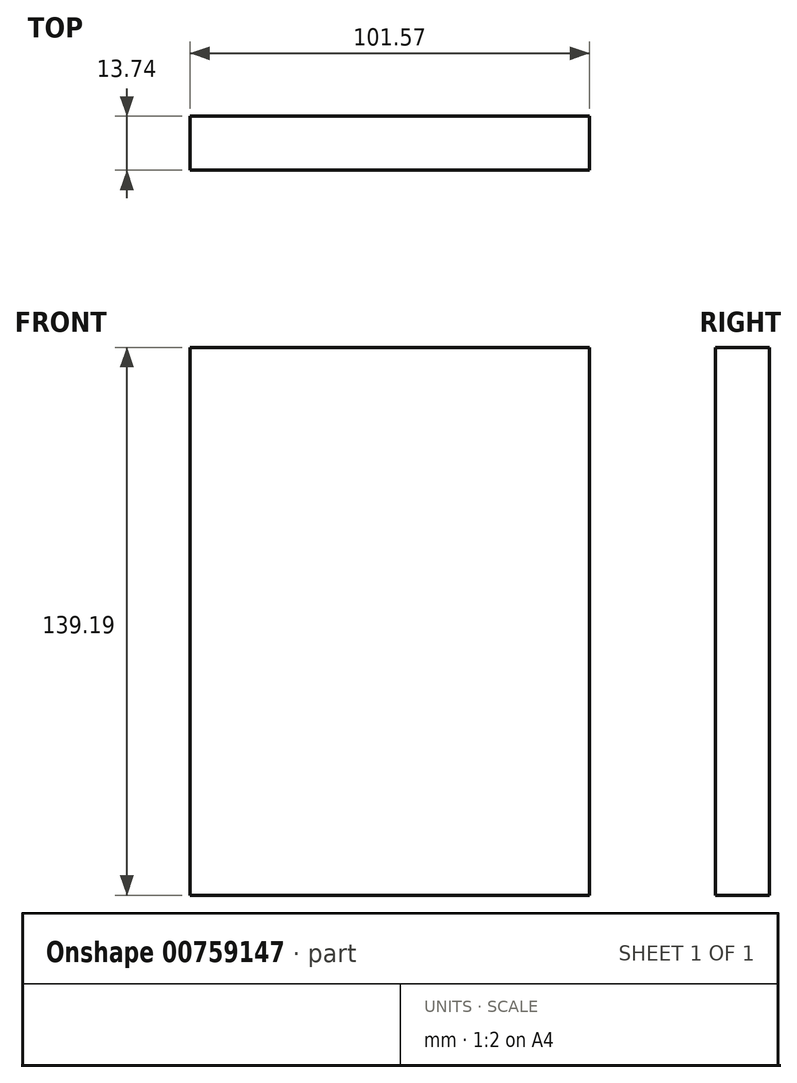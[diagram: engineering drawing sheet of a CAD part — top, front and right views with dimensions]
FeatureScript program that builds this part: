
annotation { "Feature Type Name" : "Feature", "Feature Type Description" : "" }
export const myFeature = defineFeature(function(context is Context, id is Id, definition is map)
    precondition{}
    {
        {
            var Q0;
            Q0=qCreatedBy(makeId("Top.planeOp"),FACE);
            var sketch = newSketch(context, id + "F0", { "sketchPlane" : qUnion([Q0])});
            skLineSegment(sketch, "E0.bottom", {"start": v(0, 0) * mm, "end": v(101.57, 0) * mm});
            skLineSegment(sketch, "E0.top", {"start": v(0, -13.74) * mm, "end": v(101.57, -13.74) * mm});
            skLineSegment(sketch, "E0.left", {"start": v(0, 0) * mm, "end": v(0, -13.74) * mm});
            skLineSegment(sketch, "E0.right", {"start": v(101.57, 0) * mm, "end": v(101.57, -13.74) * mm});
            skSolve(sketch);
        }
        {
            var Q0;
            Q0=makeQuery(id+"F0.imprint","IMPRINT",FACE,{"disambiguationData":[TD([[makeQuery(id+"F0.imprint","IMPRINT",EDGE,{"derivedFrom":sQuery(id+"F0.wireOp",EDGE,"E0.bottom")}),-1.0]])]});
            extrude(context, id + "F1", {"entities" : qUnion([Q0]), "depth" : 139.2 * mm, "offsetDistance" : 25.4 * mm});
        }
    });
